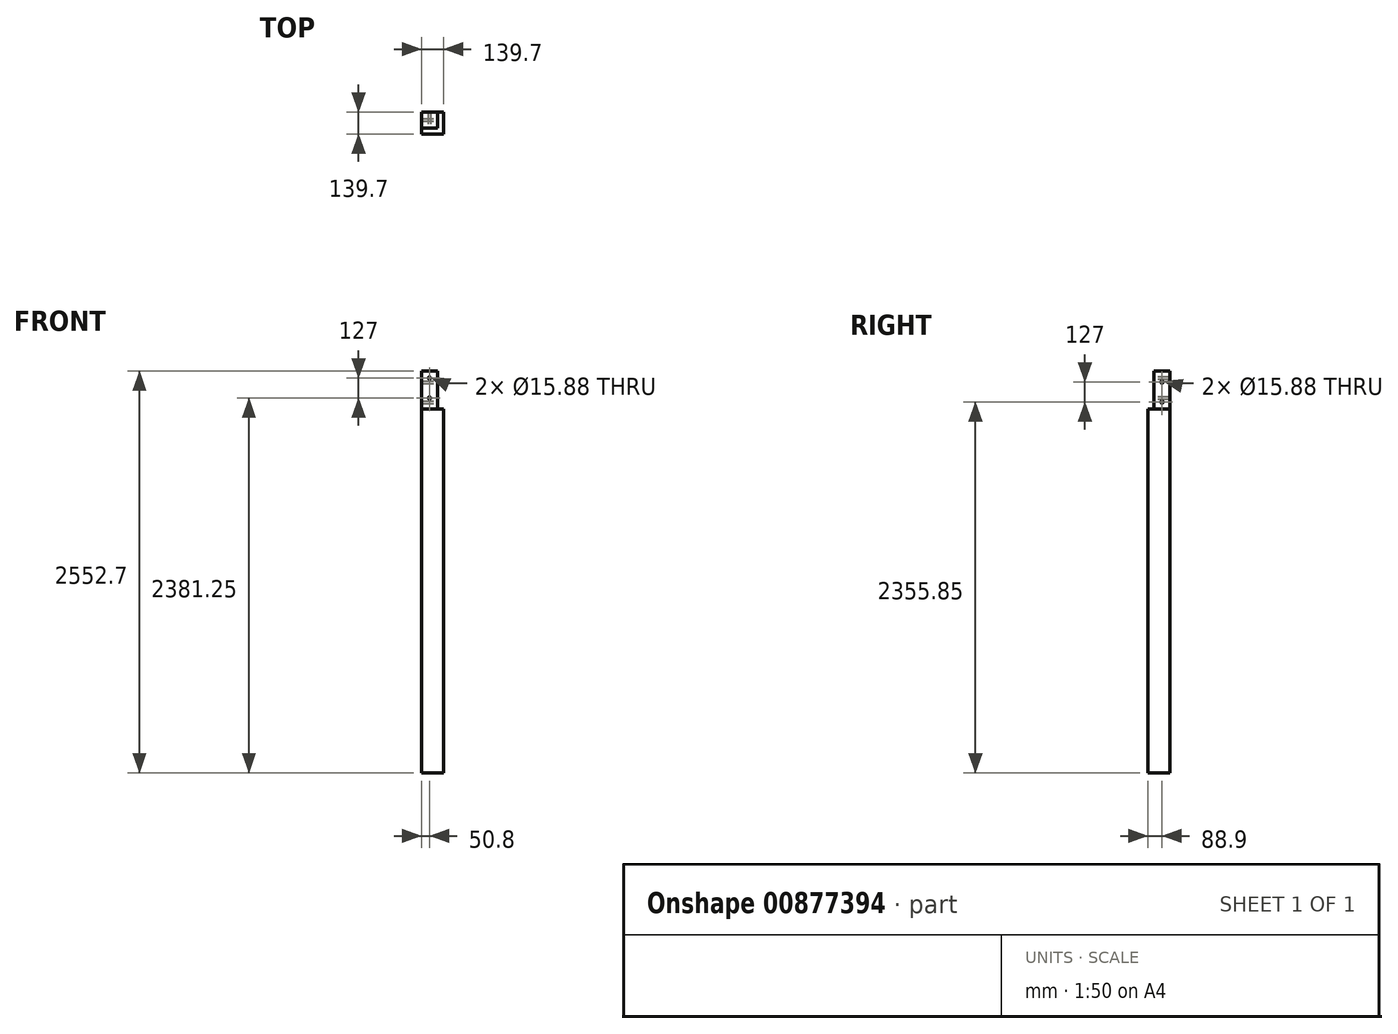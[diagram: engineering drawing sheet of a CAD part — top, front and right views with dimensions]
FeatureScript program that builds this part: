
annotation { "Feature Type Name" : "Feature", "Feature Type Description" : "" }
export const myFeature = defineFeature(function(context is Context, id is Id, definition is map)
    precondition{}
    {
        {
            var Q0;
            Q0=qCreatedBy(makeId("Top.planeOp"),FACE);
            var sketch = newSketch(context, id + "F0", { "sketchPlane" : qUnion([Q0])});
            skLineSegment(sketch, "E0.bottom", {"start": v(69.85, 69.85) * mm, "end": v(-69.85, 69.85) * mm});
            skLineSegment(sketch, "E0.top", {"start": v(69.85, -69.85) * mm, "end": v(-69.85, -69.85) * mm});
            skLineSegment(sketch, "E0.left", {"start": v(69.85, 69.85) * mm, "end": v(69.85, -69.85) * mm});
            skLineSegment(sketch, "E0.right", {"start": v(-69.85, 69.85) * mm, "end": v(-69.85, -69.85) * mm});
            skPoint(sketch, "E0.middle", {"position": v(0, 0) * mm});
            skSolve(sketch);
        }
        {
            var Q0;
            Q0=makeQuery(id+"F0.imprint","IMPRINT",FACE,{"disambiguationData":[TD([[makeQuery(id+"F0.imprint","IMPRINT",EDGE,{"derivedFrom":sQuery(id+"F0.wireOp",EDGE,"E0.bottom")}),1.0]])]});
            extrude(context, id + "F1", {"entities" : qUnion([Q0]), "oppositeDirection" : true, "depth" : 2552.7 * mm, "offsetDistance" : 25.4 * mm});
        }
        {
            var Q0;
            Q0=qCreatedBy(makeId("Front.planeOp"),FACE);
            var sketch = newSketch(context, id + "F2", { "sketchPlane" : qUnion([Q0])});
            skLineSegment(sketch, "E1.bottom", {"start": v(69.85, 0) * mm, "end": v(31.75, 0) * mm});
            skLineSegment(sketch, "E1.top", {"start": v(69.85, -241.3) * mm, "end": v(31.75, -241.3) * mm});
            skLineSegment(sketch, "E1.left", {"start": v(69.85, 0) * mm, "end": v(69.85, -241.3) * mm});
            skLineSegment(sketch, "E1.right", {"start": v(31.75, 0) * mm, "end": v(31.75, -241.3) * mm});
            skSolve(sketch);
        }
        {
            var Q0;
            Q0 = qSketchRegion(id + "F2", true);
            extrude(context, id + "F3", {"entities" : qUnion([Q0]), "operationType" : NewBodyOperationType.REMOVE, "endBound" : BoundingType.THROUGH_ALL, "depth" : 25.4 * mm, "offsetDistance" : 25.4 * mm, "hasSecondDirection" : true, "secondDirectionBound" : SecondDirectionBoundingType.THROUGH_ALL, "secondDirectionOppositeDirection" : true, "secondDirectionDepth" : 25.4 * mm});
        }
        {
            var Q0;
            Q0=qCreatedBy(makeId("Right.planeOp"),FACE);
            var sketch = newSketch(context, id + "F4", { "sketchPlane" : qUnion([Q0])});
            skLineSegment(sketch, "E2.bottom", {"start": v(-69.85, 0) * mm, "end": v(-31.75, 0) * mm});
            skLineSegment(sketch, "E2.top", {"start": v(-69.85, -241.3) * mm, "end": v(-31.75, -241.3) * mm});
            skLineSegment(sketch, "E2.left", {"start": v(-69.85, 0) * mm, "end": v(-69.85, -241.3) * mm});
            skLineSegment(sketch, "E2.right", {"start": v(-31.75, 0) * mm, "end": v(-31.75, -241.3) * mm});
            skSolve(sketch);
        }
        {
            var Q0;
            Q0 = qSketchRegion(id + "F4", true);
            extrude(context, id + "F5", {"entities" : qUnion([Q0]), "operationType" : NewBodyOperationType.REMOVE, "endBound" : BoundingType.THROUGH_ALL, "depth" : 25.4 * mm, "offsetDistance" : 25.4 * mm, "hasSecondDirection" : true, "secondDirectionBound" : SecondDirectionBoundingType.THROUGH_ALL, "secondDirectionOppositeDirection" : true, "secondDirectionDepth" : 25.4 * mm});
        }
        {
            var Q0;
            Q0=makeQuery(id+"F5.boolean.opBoolean","COPY",FACE,{"derivedFrom":makeQuery(id+"F5.opExtrude","SWEPT_FACE",FACE,{"disambiguationData":[OSD([sQuery(id+"F4.wireOp",EDGE,"E2.right")])]})});
            var sketch = newSketch(context, id + "F6", { "sketchPlane" : qUnion([Q0])});
            skLineSegment(sketch, "E3", {"start": v(-19.05, 0) * mm, "end": v(-19.05, -241.3) * mm, "construction": true});
            skLineSegment(sketch, "E4", {"start": v(-19.05, -44.45) * mm, "end": v(-19.05, -171.45) * mm});
            skPoint(sketch, "E5", {"position": v(-19.05, -107.95) * mm});
            skPoint(sketch, "E6", {"position": v(-19.05, -120.65) * mm});
            skSolve(sketch);
        }
        {
            var Q0;
            Q0=sQuery(id+"F6.wireOp",VERTEX,"E4.start");
            var Q1;
            Q1=sQuery(id+"F6.wireOp",VERTEX,"E4.end");
            var Q2;
            Q2=makeQuery(id+"F1.opExtrude","SWEPT_BODY",BODY,{"disambiguationData":[OSD([sQuery(id+"F0.wireOp",EDGE,"E0.bottom"),sQuery(id+"F0.wireOp",EDGE,"E0.top"),sQuery(id+"F0.wireOp",EDGE,"E0.left"),sQuery(id+"F0.wireOp",EDGE,"E0.right")])]});
            hole(context, id + "F7", {"style" : HoleStyle.SIMPLE, "endStyle" : HoleEndStyle.THROUGH, "holeDiameter" : 15.88 * mm, "majorDiameter" : 6.35 * mm, "isTappedThrough" : true, "tappedDepth" : 12.7 * mm, "tapClearance" : 3, "locations" : qUnion([Q0, Q1]), "scope" : qUnion([Q2])});
        }
        {
            var Q0;
            Q0=makeQuery(id+"F3.boolean.opBoolean","COPY",FACE,{"derivedFrom":makeQuery(id+"F3.opExtrude","SWEPT_FACE",FACE,{"disambiguationData":[OSD([sQuery(id+"F2.wireOp",EDGE,"E1.right")])]})});
            var sketch = newSketch(context, id + "F8", { "sketchPlane" : qUnion([Q0])});
            skLineSegment(sketch, "E7", {"start": v(19.05, 0) * mm, "end": v(19.05, -241.3) * mm, "construction": true});
            skLineSegment(sketch, "E8", {"start": v(19.05, -69.85) * mm, "end": v(19.05, -196.85) * mm});
            skPoint(sketch, "E9", {"position": v(19.05, -120.65) * mm});
            skPoint(sketch, "E10", {"position": v(19.05, -133.35) * mm});
            skSolve(sketch);
        }
        {
            var Q0;
            Q0=sQuery(id+"F8.wireOp",VERTEX,"E8.start");
            var Q1;
            Q1=sQuery(id+"F8.wireOp",VERTEX,"E8.end");
            var Q2;
            Q2=makeQuery(id+"F1.opExtrude","SWEPT_BODY",BODY,{"disambiguationData":[OSD([sQuery(id+"F0.wireOp",EDGE,"E0.bottom"),sQuery(id+"F0.wireOp",EDGE,"E0.top"),sQuery(id+"F0.wireOp",EDGE,"E0.left"),sQuery(id+"F0.wireOp",EDGE,"E0.right")])]});
            hole(context, id + "F9", {"style" : HoleStyle.SIMPLE, "endStyle" : HoleEndStyle.THROUGH, "holeDiameter" : 15.88 * mm, "majorDiameter" : 6.35 * mm, "isTappedThrough" : true, "tappedDepth" : 12.7 * mm, "tapClearance" : 3, "locations" : qUnion([Q0, Q1]), "scope" : qUnion([Q2])});
        }
    });
